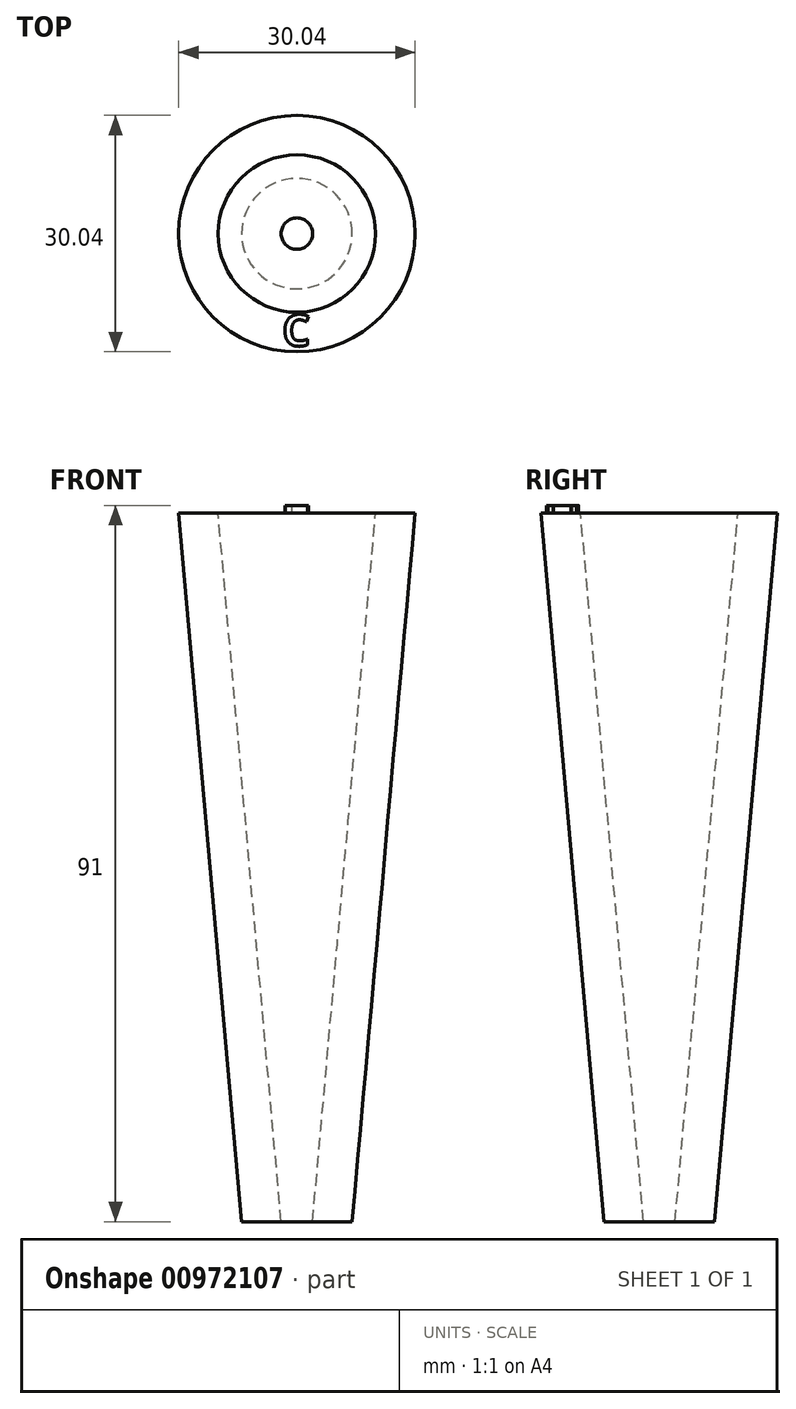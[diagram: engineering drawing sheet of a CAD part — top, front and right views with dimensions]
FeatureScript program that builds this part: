
annotation { "Feature Type Name" : "Feature", "Feature Type Description" : "" }
export const myFeature = defineFeature(function(context is Context, id is Id, definition is map)
    precondition{}
    {
        {
            var Q0;
            Q0=qCreatedBy(makeId("Front.planeOp"),FACE);
            var sketch = newSketch(context, id + "F0", { "sketchPlane" : qUnion([Q0])});
            skLineSegment(sketch, "E0", {"start": v(0, 45.38) * mm, "end": v(0, -44.62) * mm, "construction": true});
            skLineSegment(sketch, "E1", {"start": v(0, -44.62) * mm, "end": v(-2, -44.62) * mm, "construction": true});
            skLineSegment(sketch, "E2", {"start": v(0, 45.38) * mm, "end": v(-10, 45.38) * mm, "construction": true});
            skLineSegment(sketch, "E3", {"start": v(-10, 45.38) * mm, "end": v(-2, -44.62) * mm});
            skLineSegment(sketch, "E4.0", {"start": v(-14.98, 44.93) * mm, "end": v(-7.02, -44.62) * mm});
            skLineSegment(sketch, "E5", {"start": v(-2, -44.62) * mm, "end": v(-7.02, -44.62) * mm});
            skLineSegment(sketch, "E6", {"start": v(-10, 45.38) * mm, "end": v(-15.02, 45.38) * mm});
            skLineSegment(sketch, "E7", {"start": v(-14.98, 44.93) * mm, "end": v(-15.02, 45.38) * mm});
            skSolve(sketch);
        }
        {
            var Q0;
            Q0 = qSketchRegion(id + "F0", true);
            var Q1;
            Q1=sQuery(id+"F0.wireOp",EDGE,"E0");
            revolve(context, id + "F1", {"surfaceOperationType" : NewSurfaceOperationType.NEW, "entities" : qUnion([Q0]), "axis" : qUnion([Q1]), "revolveType" : RevolveType.FULL});
        }
        {
            var Q0;
            Q0=makeQuery(id+"F1.opRevolve","SWEPT_FACE",FACE,{"disambiguationData":[OSD([sQuery(id+"F0.wireOp",EDGE,"E6")])]});
            var sketch = newSketch(context, id + "F2", { "sketchPlane" : qUnion([Q0])});
            skText(sketch, "E8", { "text": "C", "fontName": "OpenSans-Bold.ttf"});
            const initialGuessF2  = {"E8": [-0.00185, -0.01427, 1, 0, 0.004]};
            skSetInitialGuess(sketch, initialGuessF2);
            skSolve(sketch);
        }
        {
            var Q0;
            Q0 = qSketchRegion(id + "F2", true);
            extrude(context, id + "F3", {"entities" : qUnion([Q0]), "operationType" : NewBodyOperationType.ADD, "depth" : 1 * mm, "offsetDistance" : 25 * mm});
        }
    });
